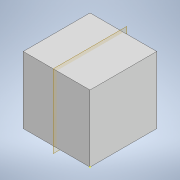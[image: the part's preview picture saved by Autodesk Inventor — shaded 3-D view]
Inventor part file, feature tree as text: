
AUTODESK INVENTOR PART (.ipt)
format: ipt  version: 2021 (Build 250183000, 183)  size: 106,496 bytes
history: native  units: in
note: dims shown in document units (in); Inventor stores cm internally (conversion verified against a paired STEP export)
features: sketch x3, extrude x2, plane x1
ambient origin geometry x8: Origin, YZ Plane, XZ Plane, XY Plane, X Axis, Y Axis, Z Axis, Center Point
bodies: Solid1 (feature_tree)
feature tree (6):
  sketch  "Sketch1"  dims[d1=0.6299in d2=0.6299in]
  extrude  "Extrusion1"  Depth=0.6299in
  plane  "Work Plane1"
  extrude  "Extrusion4"  Depth=0.6299in
  sketch  "Sketch2"  dims[d8=0.6299in d9=0.0in d39=0.1299in]
  sketch  "Sketch5"  dims[d40=0.1339in d41=0.0157in d42=0.2598in d43=0.5118in d44=0.0in]
